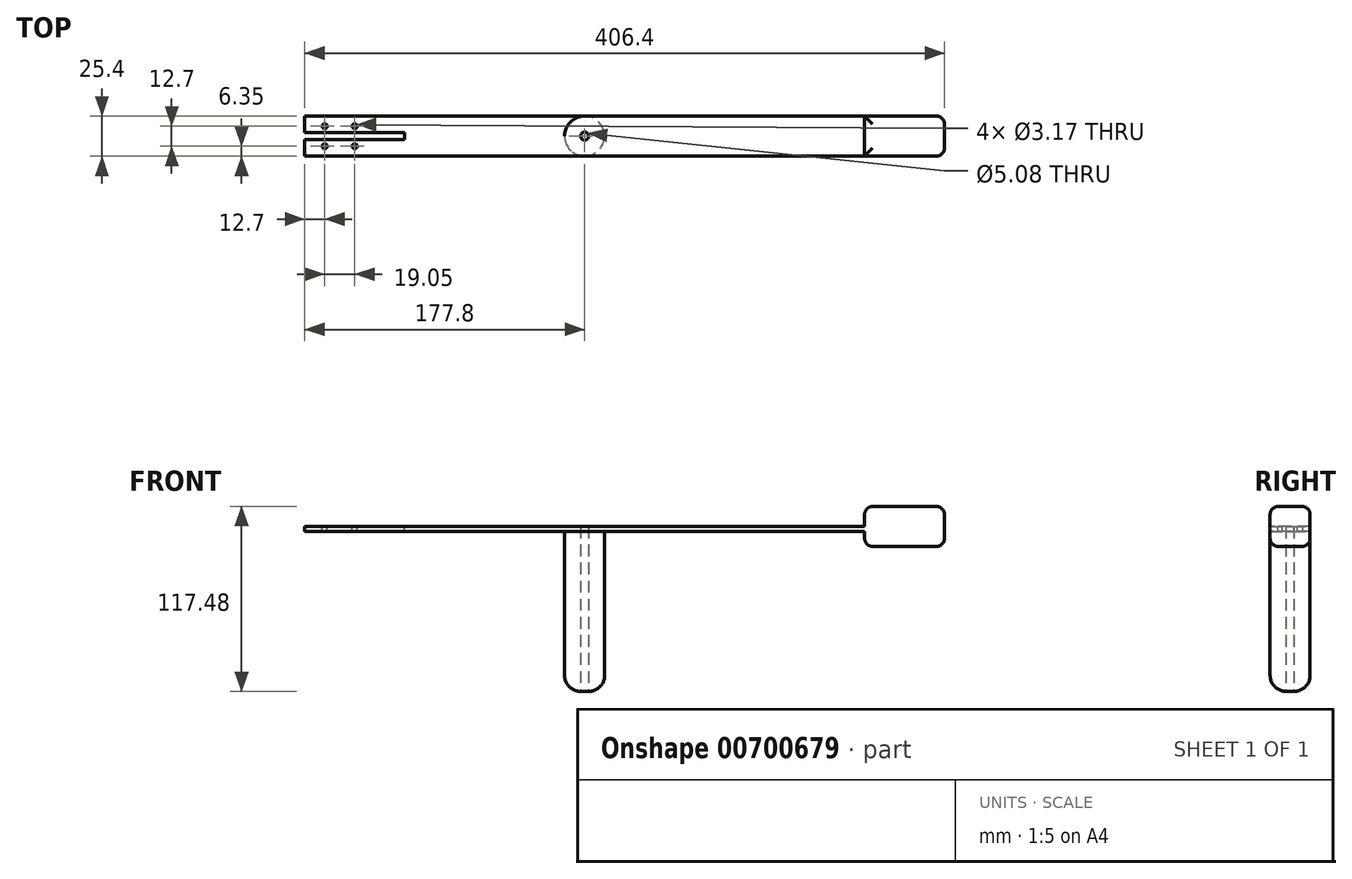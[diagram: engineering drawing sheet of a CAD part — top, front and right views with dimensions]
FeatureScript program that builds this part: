
annotation { "Feature Type Name" : "Feature", "Feature Type Description" : "" }
export const myFeature = defineFeature(function(context is Context, id is Id, definition is map)
    precondition{}
    {
        {
            var Q0;
            Q0=qCreatedBy(makeId("Front.planeOp"),FACE);
            var sketch = newSketch(context, id + "F0", { "sketchPlane" : qUnion([Q0])});
            skLineSegment(sketch, "E0.bottom", {"start": v(0, 0) * mm, "end": v(203.2, 0) * mm});
            skLineSegment(sketch, "E0.top", {"start": v(0, 3.18) * mm, "end": v(203.2, 3.18) * mm});
            skLineSegment(sketch, "E0.left", {"start": v(0, 0) * mm, "end": v(0, 3.17) * mm});
            skLineSegment(sketch, "E0.right", {"start": v(203.2, 0) * mm, "end": v(203.2, 3.18) * mm});
            skSolve(sketch);
        }
        {
            var Q0;
            Q0 = qSketchRegion(id + "F0", true);
            extrude(context, id + "F1", {"entities" : qUnion([Q0]), "depth" : 25.4 * mm, "offsetDistance" : 25.4 * mm});
        }
        {
            var Q0;
            Q0=makeQuery(id+"F1.opExtrude","SWEPT_FACE",FACE,{"disambiguationData":[OSD([sQuery(id+"F0.wireOp",EDGE,"E0.top")])]});
            var sketch = newSketch(context, id + "F2", { "sketchPlane" : qUnion([Q0])});
            skPoint(sketch, "E1", {"position": v(0, -12.7) * mm});
            skPoint(sketch, "E2", {"position": v(12.7, -12.7) * mm});
            skCircle(sketch, "E3", {"center": v(12.7, -19.05) * mm, "radius": 1.59 * mm});
            skCircle(sketch, "E4", {"center": v(12.7, -6.35) * mm, "radius": 1.59 * mm});
            skCircle(sketch, "E5", {"center": v(31.75, -6.35) * mm, "radius": 1.59 * mm});
            skCircle(sketch, "E6", {"center": v(31.75, -19.05) * mm, "radius": 1.59 * mm});
            skSolve(sketch);
        }
        {
            var Q0;
            Q0 = qSketchRegion(id + "F2", true);
            extrude(context, id + "F3", {"entities" : qUnion([Q0]), "operationType" : NewBodyOperationType.REMOVE, "oppositeDirection" : true, "depth" : 25.4 * mm, "offsetDistance" : 25.4 * mm});
        }
        {
            var Q0;
            Q0=makeQuery(id+"F1.opExtrude","SWEPT_FACE",FACE,{"disambiguationData":[OSD([sQuery(id+"F0.wireOp",EDGE,"E0.bottom")])]});
            var sketch = newSketch(context, id + "F4", { "sketchPlane" : qUnion([Q0])});
            skCircle(sketch, "E7", {"center": v(177.8, 12.7) * mm, "radius": 12.7 * mm});
            skPoint(sketch, "E8", {"position": v(177.8, 25.4) * mm});
            skPoint(sketch, "E9", {"position": v(177.8, 0) * mm});
            skSolve(sketch);
        }
        {
            var Q0;
            Q0 = qSketchRegion(id + "F4", true);
            extrude(context, id + "F5", {"entities" : qUnion([Q0]), "operationType" : NewBodyOperationType.ADD, "depth" : 101.6 * mm, "offsetDistance" : 25.4 * mm});
        }
        {
            var Q0;
            Q0=makeQuery(id+"F5.opExtrude","CAP_EDGE",EDGE,{"disambiguationData":[OSD([sQuery(id+"F4.wireOp",EDGE,"E7")])],"isStart":false});
            fillet(context, id + "F6", {"entities" : qUnion([Q0]), "radius" : 10.16 * mm, "tangentPropagation" : true, "allowEdgeOverflow" : false});
        }
        {
            var Q0;
            Q0=makeQuery(id+"F5.opExtrude","CAP_FACE",FACE,{"disambiguationData":[OSD([sQuery(id+"F4.wireOp",EDGE,"E7")])],"isStart":false});
            var sketch = newSketch(context, id + "F7", { "sketchPlane" : qUnion([Q0])});
            skCircle(sketch, "E10.0", {"center": v(177.8, 12.7) * mm, "radius": 2.54 * mm});
            skSolve(sketch);
        }
        {
            var Q0;
            Q0 = qSketchRegion(id + "F7", true);
            extrude(context, id + "F8", {"entities" : qUnion([Q0]), "operationType" : NewBodyOperationType.REMOVE, "oppositeDirection" : true, "depth" : 254 * mm, "offsetDistance" : 25.4 * mm});
        }
        {
            var Q0;
            Q0=makeQuery(id+"F1.opExtrude","SWEPT_FACE",FACE,{"disambiguationData":[OSD([sQuery(id+"F0.wireOp",EDGE,"E0.top")])]});
            var sketch = newSketch(context, id + "F9", { "sketchPlane" : qUnion([Q0])});
            skLineSegment(sketch, "E11.bottom", {"start": v(0, -14.99) * mm, "end": v(63.5, -14.99) * mm});
            skLineSegment(sketch, "E11.top", {"start": v(0, -10.41) * mm, "end": v(63.5, -10.41) * mm});
            skLineSegment(sketch, "E11.left", {"start": v(0, -14.99) * mm, "end": v(0, -10.41) * mm});
            skLineSegment(sketch, "E11.right", {"start": v(63.5, -14.99) * mm, "end": v(63.5, -10.41) * mm});
            skPoint(sketch, "E12", {"position": v(0, -12.7) * mm});
            skSolve(sketch);
        }
        {
            var Q0;
            Q0 = qSketchRegion(id + "F9", true);
            extrude(context, id + "F10", {"entities" : qUnion([Q0]), "operationType" : NewBodyOperationType.REMOVE, "oppositeDirection" : true, "depth" : 25.4 * mm, "offsetDistance" : 25.4 * mm});
        }
        {
            var Q0;
            Q0=makeQuery(id+"F1.opExtrude","SWEPT_FACE",FACE,{"disambiguationData":[OSD([sQuery(id+"F0.wireOp",EDGE,"E0.top")])]});
            var sketch = newSketch(context, id + "F11", { "sketchPlane" : qUnion([Q0])});
            skLineSegment(sketch, "E13.bottom", {"start": v(203.2, 0) * mm, "end": v(406.4, 0) * mm});
            skLineSegment(sketch, "E13.top", {"start": v(203.2, -25.4) * mm, "end": v(406.4, -25.4) * mm});
            skLineSegment(sketch, "E13.left", {"start": v(203.2, 0) * mm, "end": v(203.2, -25.4) * mm});
            skLineSegment(sketch, "E13.right", {"start": v(406.4, 0) * mm, "end": v(406.4, -25.4) * mm});
            skSolve(sketch);
        }
        {
            var Q0;
            Q0 = qSketchRegion(id + "F11", true);
            extrude(context, id + "F12", {"entities" : qUnion([Q0]), "operationType" : NewBodyOperationType.ADD, "oppositeDirection" : true, "depth" : 3.17 * mm, "offsetDistance" : 25.4 * mm});
        }
        {
            var Q0;
            Q0=makeQuery(id+"F12.boolean.opBoolean","MERGE",FACE,{"derivedFrom":[makeQuery(id+"F1.opExtrude","SWEPT_FACE",FACE,{"disambiguationData":[OSD([sQuery(id+"F0.wireOp",EDGE,"E0.top")])]}),makeQuery(id+"F12.opExtrude","CAP_FACE",FACE,{"disambiguationData":[OSD([sQuery(id+"F11.wireOp",EDGE,"E13.bottom"),sQuery(id+"F11.wireOp",EDGE,"E13.top"),sQuery(id+"F11.wireOp",EDGE,"E13.left"),sQuery(id+"F11.wireOp",EDGE,"E13.right")])],"isStart":true})]});
            var sketch = newSketch(context, id + "F13", { "sketchPlane" : qUnion([Q0])});
            skLineSegment(sketch, "E14.bottom", {"start": v(406.4, 0) * mm, "end": v(355.6, 0) * mm});
            skLineSegment(sketch, "E14.top", {"start": v(406.4, -25.4) * mm, "end": v(355.6, -25.4) * mm});
            skLineSegment(sketch, "E14.left", {"start": v(406.4, 0) * mm, "end": v(406.4, -25.4) * mm});
            skLineSegment(sketch, "E14.right", {"start": v(355.6, 0) * mm, "end": v(355.6, -25.4) * mm});
            skSolve(sketch);
        }
        {
            var Q0;
            Q0 = qSketchRegion(id + "F13", true);
            extrude(context, id + "F14", {"entities" : qUnion([Q0]), "operationType" : NewBodyOperationType.ADD, "depth" : 12.7 * mm, "offsetDistance" : 25.4 * mm});
        }
        {
            var Q0;
            Q0 = qSketchRegion(id + "F13", true);
            extrude(context, id + "F15", {"entities" : qUnion([Q0]), "operationType" : NewBodyOperationType.ADD, "oppositeDirection" : true, "depth" : 12.7 * mm, "offsetDistance" : 25.4 * mm});
        }
        {
            var Q0;
            Q0=makeQuery(id+"F14.opExtrude","CAP_EDGE",EDGE,{"disambiguationData":[OSD([sQuery(id+"F13.wireOp",EDGE,"E14.left")])],"isStart":false});
            var Q1;
            Q1=makeQuery(id+"F15.opExtrude","CAP_EDGE",EDGE,{"disambiguationData":[OSD([sQuery(id+"F13.wireOp",EDGE,"E14.left")])],"isStart":false});
            var Q2;
            Q2=makeQuery(id+"F14.opExtrude","CAP_EDGE",EDGE,{"disambiguationData":[OSD([sQuery(id+"F13.wireOp",EDGE,"E14.right")])],"isStart":false});
            var Q3;
            Q3=makeQuery(id+"F15.opExtrude","CAP_EDGE",EDGE,{"disambiguationData":[OSD([sQuery(id+"F13.wireOp",EDGE,"E14.right")])],"isStart":false});
            var Q4;
            Q4=makeQuery(id+"F14.opExtrude","CAP_EDGE",EDGE,{"disambiguationData":[OSD([sQuery(id+"F13.wireOp",EDGE,"E14.top")])],"isStart":false});
            var Q5;
            Q5=makeQuery(id+"F15.opExtrude","CAP_EDGE",EDGE,{"disambiguationData":[OSD([sQuery(id+"F13.wireOp",EDGE,"E14.top")])],"isStart":false});
            var Q6;
            Q6=makeQuery(id+"F14.opExtrude","CAP_EDGE",EDGE,{"disambiguationData":[OSD([sQuery(id+"F13.wireOp",EDGE,"E14.bottom")])],"isStart":false});
            var Q7;
            Q7=makeQuery(id+"F15.opExtrude","CAP_EDGE",EDGE,{"disambiguationData":[OSD([sQuery(id+"F13.wireOp",EDGE,"E14.bottom")])],"isStart":false});
            fillet(context, id + "F16", {"entities" : qUnion([Q0, Q1, Q2, Q3, Q4, Q5, Q6, Q7]), "radius" : 5.08 * mm, "tangentPropagation" : true, "allowEdgeOverflow" : false});
        }
        {
            var Q0;
            Q0=makeQuery(id+"F16.opFillet","BLEND_EDGE",EDGE,{"blendedFrom":[makeQuery(id+"F14.opExtrude","CAP_EDGE",EDGE,{"disambiguationData":[OSD([sQuery(id+"F13.wireOp",EDGE,"E14.top")])],"isStart":false}),makeQuery(id+"F14.opExtrude","CAP_EDGE",EDGE,{"disambiguationData":[OSD([sQuery(id+"F13.wireOp",EDGE,"E14.left")])],"isStart":false})],"blendedInto":[]});
            var Q1;
            Q1=makeQuery(id+"F16.opFillet","BLEND_EDGE",EDGE,{"blendedFrom":[makeQuery(id+"F14.opExtrude","CAP_EDGE",EDGE,{"disambiguationData":[OSD([sQuery(id+"F13.wireOp",EDGE,"E14.bottom")])],"isStart":false}),makeQuery(id+"F14.opExtrude","CAP_EDGE",EDGE,{"disambiguationData":[OSD([sQuery(id+"F13.wireOp",EDGE,"E14.left")])],"isStart":false})],"blendedInto":[]});
            fillet(context, id + "F17", {"entities" : qUnion([Q0, Q1]), "radius" : 5.08 * mm, "tangentPropagation" : true, "allowEdgeOverflow" : false});
        }
    });
